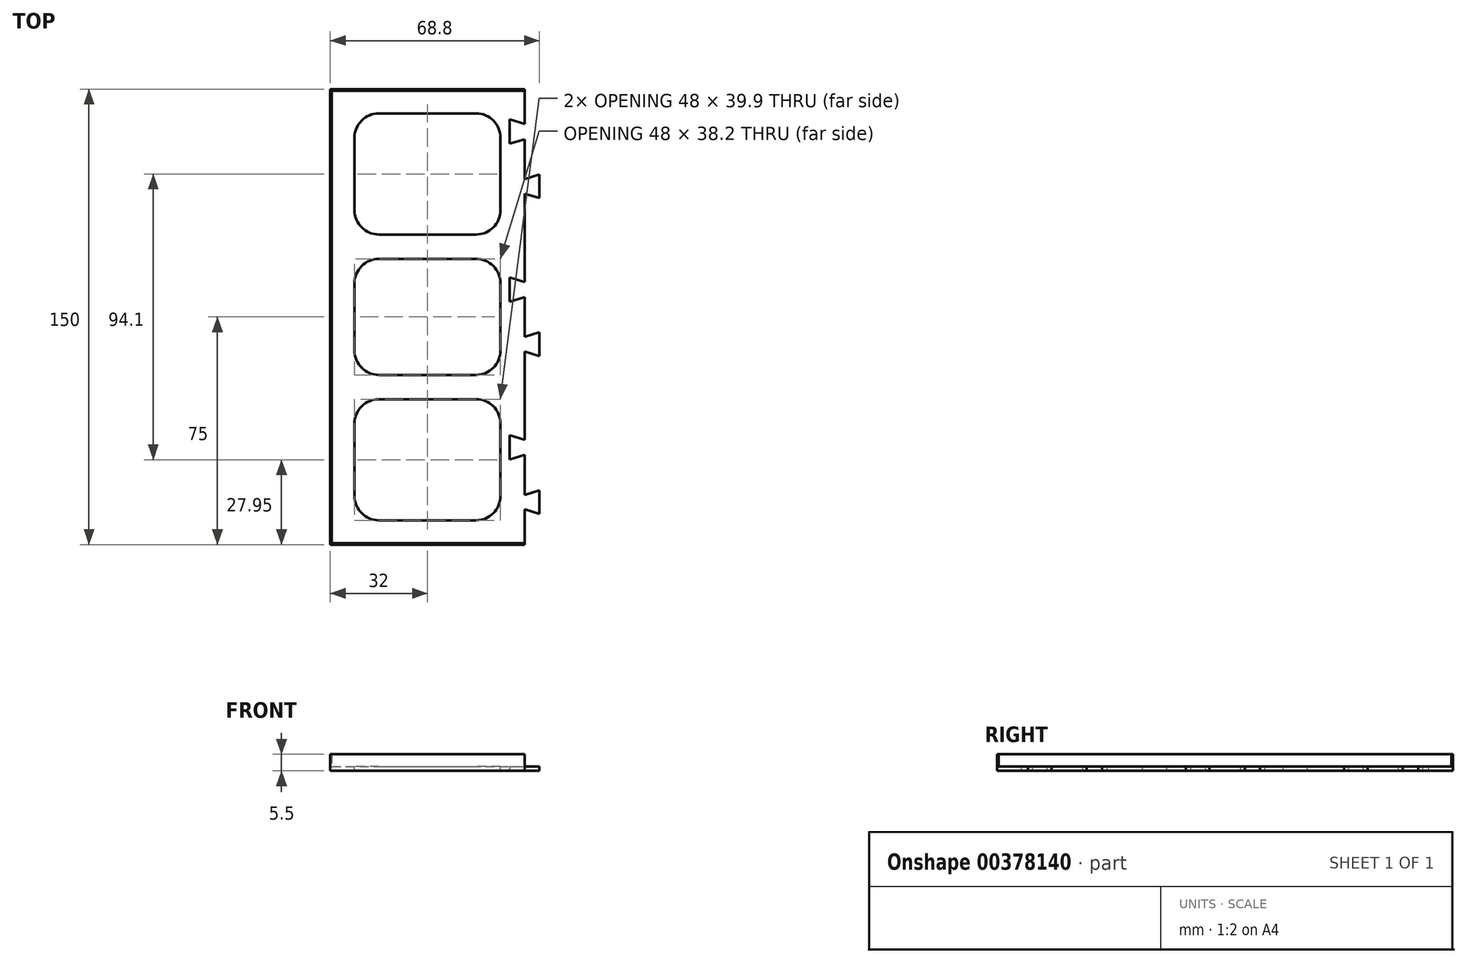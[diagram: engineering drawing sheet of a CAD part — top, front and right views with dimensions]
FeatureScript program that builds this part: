
annotation { "Feature Type Name" : "Feature", "Feature Type Description" : "" }
export const myFeature = defineFeature(function(context is Context, id is Id, definition is map)
    precondition{}
    {
        {
            var Q0;
            Q0=qCreatedBy(makeId("Top.planeOp"),FACE);
            var sketch = newSketch(context, id + "F0", { "sketchPlane" : qUnion([Q0])});
            skLineSegment(sketch, "E0", {"start": v(0, 0) * mm, "end": v(0, 150) * mm});
            skLineSegment(sketch, "E1", {"start": v(0, 150) * mm, "end": v(64, 150) * mm});
            skLineSegment(sketch, "E2", {"start": v(64, 150) * mm, "end": v(64, 138.5) * mm});
            skLineSegment(sketch, "E3", {"start": v(64, 138.5) * mm, "end": v(59, 140) * mm});
            skLineSegment(sketch, "E4", {"start": v(59, 140) * mm, "end": v(59, 132) * mm});
            skLineSegment(sketch, "E5", {"start": v(59, 132) * mm, "end": v(64, 133.5) * mm});
            skLineSegment(sketch, "E6", {"start": v(64, 133.5) * mm, "end": v(64, 120.4) * mm});
            skLineSegment(sketch, "E7", {"start": v(64, 120.4) * mm, "end": v(68.8, 121.9) * mm});
            skLineSegment(sketch, "E8", {"start": v(68.8, 121.9) * mm, "end": v(68.8, 114.1) * mm});
            skLineSegment(sketch, "E9", {"start": v(68.8, 114.1) * mm, "end": v(64, 115.6) * mm});
            skLineSegment(sketch, "E10", {"start": v(64, 115.6) * mm, "end": v(64, 86.5) * mm});
            skLineSegment(sketch, "E11", {"start": v(64, 86.5) * mm, "end": v(59, 88) * mm});
            skLineSegment(sketch, "E12", {"start": v(59, 88) * mm, "end": v(59, 80) * mm});
            skLineSegment(sketch, "E13", {"start": v(59, 80) * mm, "end": v(64, 81.5) * mm});
            skLineSegment(sketch, "E14", {"start": v(64, 81.5) * mm, "end": v(64, 68.4) * mm});
            skLineSegment(sketch, "E15", {"start": v(64, 68.4) * mm, "end": v(68.8, 69.9) * mm});
            skLineSegment(sketch, "E16", {"start": v(68.8, 69.9) * mm, "end": v(68.8, 62.1) * mm});
            skLineSegment(sketch, "E17", {"start": v(68.8, 62.1) * mm, "end": v(64, 63.6) * mm});
            skLineSegment(sketch, "E18", {"start": v(64, 63.6) * mm, "end": v(64, 34.5) * mm});
            skLineSegment(sketch, "E19", {"start": v(64, 34.5) * mm, "end": v(59, 36) * mm});
            skLineSegment(sketch, "E20", {"start": v(59, 36) * mm, "end": v(59, 28) * mm});
            skLineSegment(sketch, "E21", {"start": v(59, 28) * mm, "end": v(64, 29.5) * mm});
            skLineSegment(sketch, "E22", {"start": v(64, 29.5) * mm, "end": v(64, 16.4) * mm});
            skLineSegment(sketch, "E23", {"start": v(64, 16.4) * mm, "end": v(68.8, 17.9) * mm});
            skLineSegment(sketch, "E24", {"start": v(68.8, 17.9) * mm, "end": v(68.8, 10.1) * mm});
            skLineSegment(sketch, "E25", {"start": v(68.8, 10.1) * mm, "end": v(64, 11.6) * mm});
            skLineSegment(sketch, "E26", {"start": v(64, 11.6) * mm, "end": v(64, 0) * mm});
            skLineSegment(sketch, "E27", {"start": v(64, 0) * mm, "end": v(0, 0) * mm});
            skSolve(sketch);
        }
        {
            var Q0;
            Q0=makeQuery(id+"F0.imprint","IMPRINT",FACE,{"disambiguationData":[TD([[makeQuery(id+"F0.imprint","IMPRINT",EDGE,{"derivedFrom":sQuery(id+"F0.wireOp",EDGE,"E0")}),-1.0]])]});
            extrude(context, id + "F1", {"entities" : qUnion([Q0]), "depth" : 1.5 * mm});
        }
        {
            var Q0;
            Q0=makeQuery(id+"F1.opExtrude","CAP_FACE",FACE,{"disambiguationData":[OSD([sQuery(id+"F0.wireOp",EDGE,"E0"),sQuery(id+"F0.wireOp",EDGE,"E1"),sQuery(id+"F0.wireOp",EDGE,"E2"),sQuery(id+"F0.wireOp",EDGE,"E3"),sQuery(id+"F0.wireOp",EDGE,"E4"),sQuery(id+"F0.wireOp",EDGE,"E5"),sQuery(id+"F0.wireOp",EDGE,"E6"),sQuery(id+"F0.wireOp",EDGE,"E7"),sQuery(id+"F0.wireOp",EDGE,"E8"),sQuery(id+"F0.wireOp",EDGE,"E9"),sQuery(id+"F0.wireOp",EDGE,"E10"),sQuery(id+"F0.wireOp",EDGE,"E11"),sQuery(id+"F0.wireOp",EDGE,"E12"),sQuery(id+"F0.wireOp",EDGE,"E13"),sQuery(id+"F0.wireOp",EDGE,"E14"),sQuery(id+"F0.wireOp",EDGE,"E15"),sQuery(id+"F0.wireOp",EDGE,"E16"),sQuery(id+"F0.wireOp",EDGE,"E17"),sQuery(id+"F0.wireOp",EDGE,"E18"),sQuery(id+"F0.wireOp",EDGE,"E19"),sQuery(id+"F0.wireOp",EDGE,"E20"),sQuery(id+"F0.wireOp",EDGE,"E21"),sQuery(id+"F0.wireOp",EDGE,"E22"),sQuery(id+"F0.wireOp",EDGE,"E23"),sQuery(id+"F0.wireOp",EDGE,"E24"),sQuery(id+"F0.wireOp",EDGE,"E25"),sQuery(id+"F0.wireOp",EDGE,"E26"),sQuery(id+"F0.wireOp",EDGE,"E27")])],"isStart":false});
            var sketch = newSketch(context, id + "F2", { "sketchPlane" : qUnion([Q0])});
            skLineSegment(sketch, "E28.bottom", {"start": v(8, 47.9) * mm, "end": v(56, 47.9) * mm});
            skLineSegment(sketch, "E28.top", {"start": v(8, 8) * mm, "end": v(56, 8) * mm});
            skLineSegment(sketch, "E28.left", {"start": v(8, 47.9) * mm, "end": v(8, 8) * mm});
            skLineSegment(sketch, "E28.right", {"start": v(56, 47.9) * mm, "end": v(56, 8) * mm});
            skLineSegment(sketch, "E29.bottom", {"start": v(8, 94.1) * mm, "end": v(56, 94.1) * mm});
            skLineSegment(sketch, "E29.top", {"start": v(8, 55.9) * mm, "end": v(56, 55.9) * mm});
            skLineSegment(sketch, "E29.left", {"start": v(8, 94.1) * mm, "end": v(8, 55.9) * mm});
            skLineSegment(sketch, "E29.right", {"start": v(56, 94.1) * mm, "end": v(56, 55.9) * mm});
            skLineSegment(sketch, "E30.bottom", {"start": v(8, 142) * mm, "end": v(56, 142) * mm});
            skLineSegment(sketch, "E30.top", {"start": v(8, 102.1) * mm, "end": v(56, 102.1) * mm});
            skLineSegment(sketch, "E30.left", {"start": v(8, 142) * mm, "end": v(8, 102.1) * mm});
            skLineSegment(sketch, "E30.right", {"start": v(56, 142) * mm, "end": v(56, 102.1) * mm});
            skSolve(sketch);
        }
        {
            var Q0;
            Q0=makeQuery(id+"F2.imprint","IMPRINT",FACE,{"disambiguationData":[TD([[makeQuery(id+"F2.imprint","IMPRINT",EDGE,{"derivedFrom":sQuery(id+"F2.wireOp",EDGE,"E30.bottom")}),-1.0]])]});
            var Q1;
            Q1=makeQuery(id+"F2.imprint","IMPRINT",FACE,{"disambiguationData":[TD([[makeQuery(id+"F2.imprint","IMPRINT",EDGE,{"derivedFrom":sQuery(id+"F2.wireOp",EDGE,"E29.bottom")}),-1.0]])]});
            var Q2;
            Q2=makeQuery(id+"F2.imprint","IMPRINT",FACE,{"disambiguationData":[TD([[makeQuery(id+"F2.imprint","IMPRINT",EDGE,{"derivedFrom":sQuery(id+"F2.wireOp",EDGE,"E28.bottom")}),-1.0]])]});
            extrude(context, id + "F3", {"entities" : qUnion([Q0, Q1, Q2]), "operationType" : NewBodyOperationType.REMOVE, "endBound" : BoundingType.THROUGH_ALL, "oppositeDirection" : true, "depth" : 25 * mm});
        }
        {
            var Q0;
            Q0=makeQuery(id+"F3.boolean.opBoolean","COPY",EDGE,{"derivedFrom":makeQuery(id+"F3.opExtrude","SWEPT_EDGE",EDGE,{"disambiguationData":[OSD([sQuery(id+"F2.wireOp",EDGE,"E30.bottom"),sQuery(id+"F2.wireOp",EDGE,"E30.left")])]})});
            var Q1;
            Q1=makeQuery(id+"F3.boolean.opBoolean","COPY",EDGE,{"derivedFrom":makeQuery(id+"F3.opExtrude","SWEPT_EDGE",EDGE,{"disambiguationData":[OSD([sQuery(id+"F2.wireOp",EDGE,"E29.bottom"),sQuery(id+"F2.wireOp",EDGE,"E29.left")])]})});
            var Q2;
            Q2=makeQuery(id+"F3.boolean.opBoolean","COPY",EDGE,{"derivedFrom":makeQuery(id+"F3.opExtrude","SWEPT_EDGE",EDGE,{"disambiguationData":[OSD([sQuery(id+"F2.wireOp",EDGE,"E28.bottom"),sQuery(id+"F2.wireOp",EDGE,"E28.left")])]})});
            var Q3;
            Q3=makeQuery(id+"F3.boolean.opBoolean","COPY",EDGE,{"derivedFrom":makeQuery(id+"F3.opExtrude","SWEPT_EDGE",EDGE,{"disambiguationData":[OSD([sQuery(id+"F2.wireOp",EDGE,"E30.bottom"),sQuery(id+"F2.wireOp",EDGE,"E30.right")])]})});
            var Q4;
            Q4=makeQuery(id+"F3.boolean.opBoolean","COPY",EDGE,{"derivedFrom":makeQuery(id+"F3.opExtrude","SWEPT_EDGE",EDGE,{"disambiguationData":[OSD([sQuery(id+"F2.wireOp",EDGE,"E29.bottom"),sQuery(id+"F2.wireOp",EDGE,"E29.right")])]})});
            var Q5;
            Q5=makeQuery(id+"F3.boolean.opBoolean","COPY",EDGE,{"derivedFrom":makeQuery(id+"F3.opExtrude","SWEPT_EDGE",EDGE,{"disambiguationData":[OSD([sQuery(id+"F2.wireOp",EDGE,"E28.bottom"),sQuery(id+"F2.wireOp",EDGE,"E28.right")])]})});
            var Q6;
            Q6=makeQuery(id+"F3.boolean.opBoolean","COPY",EDGE,{"derivedFrom":makeQuery(id+"F3.opExtrude","SWEPT_EDGE",EDGE,{"disambiguationData":[OSD([sQuery(id+"F2.wireOp",EDGE,"E30.top"),sQuery(id+"F2.wireOp",EDGE,"E30.right")])]})});
            var Q7;
            Q7=makeQuery(id+"F3.boolean.opBoolean","COPY",EDGE,{"derivedFrom":makeQuery(id+"F3.opExtrude","SWEPT_EDGE",EDGE,{"disambiguationData":[OSD([sQuery(id+"F2.wireOp",EDGE,"E29.top"),sQuery(id+"F2.wireOp",EDGE,"E29.right")])]})});
            var Q8;
            Q8=makeQuery(id+"F3.boolean.opBoolean","COPY",EDGE,{"derivedFrom":makeQuery(id+"F3.opExtrude","SWEPT_EDGE",EDGE,{"disambiguationData":[OSD([sQuery(id+"F2.wireOp",EDGE,"E28.top"),sQuery(id+"F2.wireOp",EDGE,"E28.right")])]})});
            var Q9;
            Q9=makeQuery(id+"F3.boolean.opBoolean","COPY",EDGE,{"derivedFrom":makeQuery(id+"F3.opExtrude","SWEPT_EDGE",EDGE,{"disambiguationData":[OSD([sQuery(id+"F2.wireOp",EDGE,"E28.top"),sQuery(id+"F2.wireOp",EDGE,"E28.left")])]})});
            var Q10;
            Q10=makeQuery(id+"F3.boolean.opBoolean","COPY",EDGE,{"derivedFrom":makeQuery(id+"F3.opExtrude","SWEPT_EDGE",EDGE,{"disambiguationData":[OSD([sQuery(id+"F2.wireOp",EDGE,"E29.top"),sQuery(id+"F2.wireOp",EDGE,"E29.left")])]})});
            var Q11;
            Q11=makeQuery(id+"F3.boolean.opBoolean","COPY",EDGE,{"derivedFrom":makeQuery(id+"F3.opExtrude","SWEPT_EDGE",EDGE,{"disambiguationData":[OSD([sQuery(id+"F2.wireOp",EDGE,"E30.top"),sQuery(id+"F2.wireOp",EDGE,"E30.left")])]})});
            fillet(context, id + "F4", {"entities" : qUnion([Q0, Q1, Q2, Q3, Q4, Q5, Q6, Q7, Q8, Q9, Q10, Q11]), "radius" : 8 * mm, "tangentPropagation" : true, "allowEdgeOverflow" : false});
        }
        {
            var Q0;
            Q0=makeQuery(id+"F1.opExtrude","CAP_FACE",FACE,{"disambiguationData":[OSD([sQuery(id+"F0.wireOp",EDGE,"E0"),sQuery(id+"F0.wireOp",EDGE,"E1"),sQuery(id+"F0.wireOp",EDGE,"E2"),sQuery(id+"F0.wireOp",EDGE,"E3"),sQuery(id+"F0.wireOp",EDGE,"E4"),sQuery(id+"F0.wireOp",EDGE,"E5"),sQuery(id+"F0.wireOp",EDGE,"E6"),sQuery(id+"F0.wireOp",EDGE,"E7"),sQuery(id+"F0.wireOp",EDGE,"E8"),sQuery(id+"F0.wireOp",EDGE,"E9"),sQuery(id+"F0.wireOp",EDGE,"E10"),sQuery(id+"F0.wireOp",EDGE,"E11"),sQuery(id+"F0.wireOp",EDGE,"E12"),sQuery(id+"F0.wireOp",EDGE,"E13"),sQuery(id+"F0.wireOp",EDGE,"E14"),sQuery(id+"F0.wireOp",EDGE,"E15"),sQuery(id+"F0.wireOp",EDGE,"E16"),sQuery(id+"F0.wireOp",EDGE,"E17"),sQuery(id+"F0.wireOp",EDGE,"E18"),sQuery(id+"F0.wireOp",EDGE,"E19"),sQuery(id+"F0.wireOp",EDGE,"E20"),sQuery(id+"F0.wireOp",EDGE,"E21"),sQuery(id+"F0.wireOp",EDGE,"E22"),sQuery(id+"F0.wireOp",EDGE,"E23"),sQuery(id+"F0.wireOp",EDGE,"E24"),sQuery(id+"F0.wireOp",EDGE,"E25"),sQuery(id+"F0.wireOp",EDGE,"E26"),sQuery(id+"F0.wireOp",EDGE,"E27")])],"isStart":false});
            var sketch = newSketch(context, id + "F5", { "sketchPlane" : qUnion([Q0])});
            skLineSegment(sketch, "E31", {"start": v(64, 150) * mm, "end": v(0, 150) * mm});
            skLineSegment(sketch, "E32", {"start": v(0, 150) * mm, "end": v(0, 0) * mm});
            skLineSegment(sketch, "E33", {"start": v(0, 0) * mm, "end": v(64, 0) * mm});
            skLineSegment(sketch, "E34", {"start": v(64, 0) * mm, "end": v(64, 0.5) * mm});
            skLineSegment(sketch, "E35", {"start": v(64, 0.5) * mm, "end": v(0.5, 0.5) * mm});
            skLineSegment(sketch, "E36", {"start": v(0.5, 0.5) * mm, "end": v(0.5, 149.5) * mm});
            skLineSegment(sketch, "E37", {"start": v(0.5, 149.5) * mm, "end": v(64, 149.5) * mm});
            skLineSegment(sketch, "E38", {"start": v(64, 149.5) * mm, "end": v(64, 150) * mm});
            skSolve(sketch);
        }
        {
            var Q0;
            Q0=makeQuery(id+"F5.imprint","IMPRINT",FACE,{"disambiguationData":[TD([[makeQuery(id+"F5.imprint","IMPRINT",EDGE,{"derivedFrom":sQuery(id+"F5.wireOp",EDGE,"E31")}),-1.0]])]});
            extrude(context, id + "F6", {"entities" : qUnion([Q0]), "operationType" : NewBodyOperationType.ADD, "depth" : 4 * mm});
        }
    });
